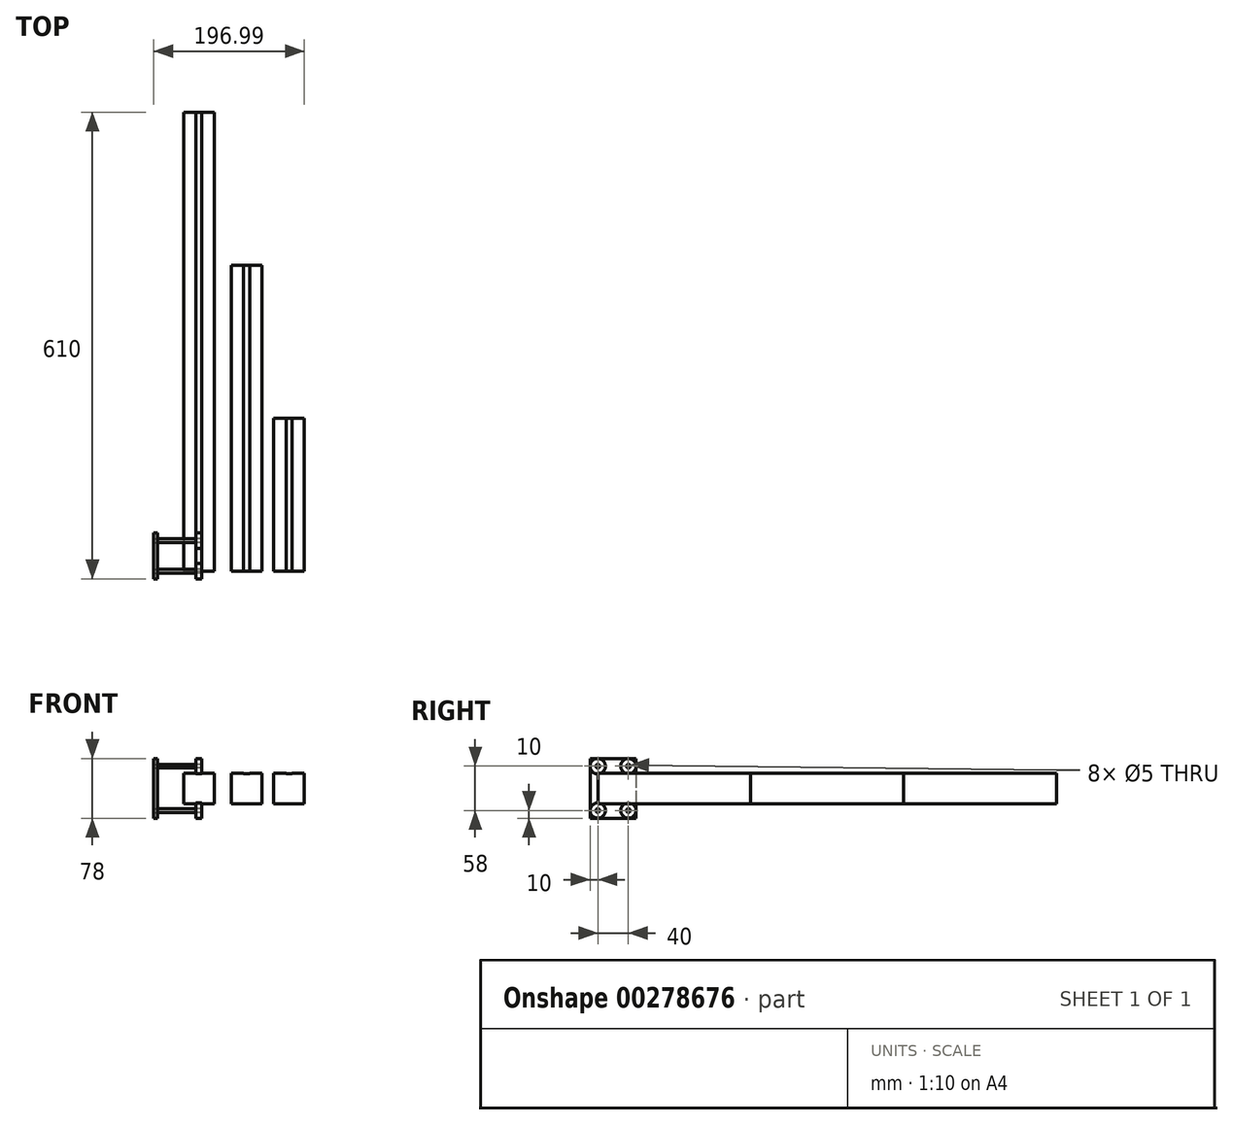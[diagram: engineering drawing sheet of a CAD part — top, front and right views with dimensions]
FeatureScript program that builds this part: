
annotation { "Feature Type Name" : "Feature", "Feature Type Description" : "" }
export const myFeature = defineFeature(function(context is Context, id is Id, definition is map)
    precondition{}
    {
        {
            var Q0;
            Q0=qCreatedBy(makeId("Front.planeOp"),FACE);
            var sketch = newSketch(context, id + "F0", { "sketchPlane" : qUnion([Q0])});
            skLineSegment(sketch, "E0.bottom", {"start": v(-20, 20) * mm, "end": v(-4, 20) * mm});
            skLineSegment(sketch, "E0.top", {"start": v(-20, -20) * mm, "end": v(20, -20) * mm});
            skLineSegment(sketch, "E0.left", {"start": v(-20, 20) * mm, "end": v(-20, -20) * mm});
            skLineSegment(sketch, "E0.right", {"start": v(20, 20) * mm, "end": v(20, -20) * mm});
            skPoint(sketch, "E0.middle", {"position": v(0, 0) * mm});
            skLineSegment(sketch, "E1", {"start": v(-4, 19) * mm, "end": v(4, 19) * mm});
            skPoint(sketch, "E2", {"position": v(0, 19) * mm});
            skPoint(sketch, "E2.positionSnap0", {"position": v(0, 20) * mm});
            skLineSegment(sketch, "E3", {"start": v(-4, 19) * mm, "end": v(-4, 20) * mm});
            skLineSegment(sketch, "E4", {"start": v(4, 19) * mm, "end": v(4, 20) * mm});
            skLineSegment(sketch, "E5.trimOffspring", {"start": v(4, 20) * mm, "end": v(20, 20) * mm});
            skLineSegment(sketch, "E6.bottom", {"start": v(-82.6, 20) * mm, "end": v(-66.6, 20) * mm});
            skLineSegment(sketch, "E6.top", {"start": v(-82.6, -20) * mm, "end": v(-42.6, -20) * mm});
            skLineSegment(sketch, "E6.left", {"start": v(-82.6, 20) * mm, "end": v(-82.6, -20) * mm});
            skLineSegment(sketch, "E6.right", {"start": v(-42.6, 20) * mm, "end": v(-42.6, -20) * mm});
            skPoint(sketch, "E6.middle", {"position": v(-62.6, 0) * mm});
            skLineSegment(sketch, "E7", {"start": v(-66.6, 19) * mm, "end": v(-58.6, 19) * mm});
            skPoint(sketch, "E8", {"position": v(-62.6, 19) * mm});
            skPoint(sketch, "E8.positionSnap0", {"position": v(-62.6, 20) * mm});
            skLineSegment(sketch, "E9", {"start": v(-66.6, 19) * mm, "end": v(-66.6, 20) * mm});
            skLineSegment(sketch, "E10", {"start": v(-58.6, 19) * mm, "end": v(-58.6, 20) * mm});
            skLineSegment(sketch, "E11.trimOffspring", {"start": v(-58.6, 20) * mm, "end": v(-42.6, 20) * mm});
            skLineSegment(sketch, "E12.bottom", {"start": v(35.4, 20) * mm, "end": v(51.4, 20) * mm});
            skLineSegment(sketch, "E12.top", {"start": v(35.4, -20) * mm, "end": v(75.4, -20) * mm});
            skLineSegment(sketch, "E12.left", {"start": v(35.4, 20) * mm, "end": v(35.4, -20) * mm});
            skLineSegment(sketch, "E12.right", {"start": v(75.4, 20) * mm, "end": v(75.4, -20) * mm});
            skPoint(sketch, "E12.middle", {"position": v(55.4, 0) * mm});
            skLineSegment(sketch, "E13", {"start": v(51.4, 19) * mm, "end": v(59.4, 19) * mm});
            skPoint(sketch, "E14", {"position": v(55.4, 19) * mm});
            skPoint(sketch, "E14.positionSnap0", {"position": v(55.4, 20) * mm});
            skLineSegment(sketch, "E15", {"start": v(51.4, 19) * mm, "end": v(51.4, 20) * mm});
            skLineSegment(sketch, "E16", {"start": v(59.4, 19) * mm, "end": v(59.4, 20) * mm});
            skLineSegment(sketch, "E17.trimOffspring", {"start": v(59.4, 20) * mm, "end": v(75.4, 20) * mm});
            skSolve(sketch);
        }
        {
            var Q0;
            Q0=makeQuery(id+"F0.imprint","IMPRINT",FACE,{"disambiguationData":[TD([[makeQuery(id+"F0.imprint","IMPRINT",EDGE,{"derivedFrom":sQuery(id+"F0.wireOp",EDGE,"E6.bottom")}),-1.0]])]});
            extrude(context, id + "F1", {"entities" : qUnion([Q0]), "oppositeDirection" : true, "depth" : 600 * mm});
        }
        {
            var Q0;
            Q0=makeQuery(id+"F0.imprint","IMPRINT",FACE,{"disambiguationData":[TD([[makeQuery(id+"F0.imprint","IMPRINT",EDGE,{"derivedFrom":sQuery(id+"F0.wireOp",EDGE,"E0.bottom")}),-1.0]])]});
            extrude(context, id + "F2", {"entities" : qUnion([Q0]), "oppositeDirection" : true, "depth" : 400 * mm});
        }
        {
            var Q0;
            Q0=makeQuery(id+"F0.imprint","IMPRINT",FACE,{"disambiguationData":[TD([[makeQuery(id+"F0.imprint","IMPRINT",EDGE,{"derivedFrom":sQuery(id+"F0.wireOp",EDGE,"E12.bottom")}),-1.0]])]});
            extrude(context, id + "F3", {"entities" : qUnion([Q0]), "oppositeDirection" : true, "depth" : 200 * mm});
        }
        {
            var Q0;
            Q0=makeQuery(id+"F0.imprint","IMPRINT",FACE,{"disambiguationData":[TD([[makeQuery(id+"F0.imprint","IMPRINT",EDGE,{"derivedFrom":sQuery(id+"F0.wireOp",EDGE,"E6.bottom")}),-1.0]])]});
            var sketch = newSketch(context, id + "F4", { "sketchPlane" : qUnion([Q0])});
            skLineSegment(sketch, "E18", {"start": v(-69.2, 29) * mm, "end": v(-55.7, 29) * mm, "construction": true});
            skLineSegment(sketch, "E19", {"start": v(-66.6, 19) * mm, "end": v(-66.6, 26.5) * mm});
            skLineSegment(sketch, "E20", {"start": v(-58.6, 26.5) * mm, "end": v(-58.6, 19) * mm});
            skLineSegment(sketch, "E21", {"start": v(-66.6, 19) * mm, "end": v(-58.6, 19) * mm});
            skLineSegment(sketch, "E22", {"start": v(-66.6, 26.5) * mm, "end": v(-58.6, 26.5) * mm});
            skPoint(sketch, "E23.orphan", {"position": v(-58.6, 29) * mm});
            skSolve(sketch);
        }
        {
            var Q0;
            {var subQ0=sQuery(id+"F4.wireOp",EDGE,"E21");Q0=makeQuery(id+"F4.imprint","IMPRINT",FACE,{"disambiguationData":[TD([[makeQuery(id+"F4.imprint","IMPRINT",EDGE,{"derivedFrom":subQ0}),1.0]])]});}
            var Q1;
            Q1=sQuery(id+"F4.wireOp",EDGE,"E18");
            revolve(context, id + "F5", {"entities" : qUnion([Q0]), "axis" : qUnion([Q1]), "revolveType" : RevolveType.FULL});
        }
        {
            var Q0;
            Q0=makeQuery(id+"F5.opRevolve","SWEPT_FACE",FACE,{"disambiguationData":[OSD([sQuery(id+"F4.wireOp",EDGE,"E19")])]});
            var sketch = newSketch(context, id + "F6", { "sketchPlane" : qUnion([Q0])});
            skCircle(sketch, "E24.0.0", {"center": v(0, 29) * mm, "radius": 10 * mm});
            skSolve(sketch);
        }
        {
            var Q0;
            Q0=makeQuery(id+"F6.imprint","IMPRINT",FACE,{"disambiguationData":[TD([[makeQuery(id+"F6.imprint","IMPRINT",EDGE,{"derivedFrom":makeQuery(id+"F5.opRevolve","SWEPT_EDGE",EDGE,{"disambiguationData":[OSD([sQuery(id+"F4.wireOp",EDGE,"E19"),sQuery(id+"F4.wireOp",EDGE,"E22")])]})}),1.0]])]});
            extrude(context, id + "F7", {"entities" : qUnion([Q0]), "depth" : 50 * mm});
        }
        {
            var Q0;
            Q0=makeQuery(id+"F7.opExtrude","SWEPT_BODY",BODY,{"disambiguationData":[OSD([sQuery(id+"F4.wireOp",EDGE,"E19"),sQuery(id+"F4.wireOp",EDGE,"E22")])]});
            var Q1;
            Q1=makeQuery(id+"F5.opRevolve","SWEPT_BODY",BODY,{"disambiguationData":[OSD([sQuery(id+"F4.wireOp",EDGE,"E19"),sQuery(id+"F4.wireOp",EDGE,"E20"),sQuery(id+"F4.wireOp",EDGE,"E21"),sQuery(id+"F4.wireOp",EDGE,"E22")])]});
            var Q2;
            Q2=qCreatedBy(makeId("Top.planeOp"),FACE);
            mirror(context, id + "F8", {"entities" : qUnion([Q0, Q1]), "mirrorPlane" : qUnion([Q2])});
        }
        {
            var Q0;
            Q0=makeQuery(id+"F5.opRevolve","SWEPT_BODY",BODY,{"disambiguationData":[OSD([sQuery(id+"F4.wireOp",EDGE,"E19"),sQuery(id+"F4.wireOp",EDGE,"E20"),sQuery(id+"F4.wireOp",EDGE,"E21"),sQuery(id+"F4.wireOp",EDGE,"E22")])]});
            var Q1;
            Q1=makeQuery(id+"F7.opExtrude","SWEPT_BODY",BODY,{"disambiguationData":[OSD([sQuery(id+"F4.wireOp",EDGE,"E19"),sQuery(id+"F4.wireOp",EDGE,"E22")])]});
            var Q2;
            Q2=makeQuery(id+"F8.opPattern","COPY",BODY,{"derivedFrom":makeQuery(id+"F7.opExtrude","SWEPT_BODY",BODY,{"disambiguationData":[OSD([sQuery(id+"F4.wireOp",EDGE,"E19"),sQuery(id+"F4.wireOp",EDGE,"E22")])]}),"instanceName":"1"});
            var Q3;
            Q3=makeQuery(id+"F8.opPattern","COPY",BODY,{"derivedFrom":makeQuery(id+"F5.opRevolve","SWEPT_BODY",BODY,{"disambiguationData":[OSD([sQuery(id+"F4.wireOp",EDGE,"E19"),sQuery(id+"F4.wireOp",EDGE,"E20"),sQuery(id+"F4.wireOp",EDGE,"E21"),sQuery(id+"F4.wireOp",EDGE,"E22")])]}),"instanceName":"1"});
            var Q4;
            Q4=makeQuery(id+"F1.opExtrude","SWEPT_EDGE",EDGE,{"disambiguationData":[OSD([sQuery(id+"F0.wireOp",EDGE,"E6.bottom"),sQuery(id+"F0.wireOp",EDGE,"E6.left")])]});
            transform(context, id + "F9", {"entities" : qUnion([Q0, Q1, Q2, Q3]), "transformType" : TransformType.TRANSLATION_DISTANCE, "transformDirection" : qUnion([Q4]), "distance" : 40 * mm, "oppositeDirection" : true, "makeCopy" : true});
        }
        {
            var Q0;
            Q0=makeQuery(id+"F9.opPattern","COPY",FACE,{"derivedFrom":makeQuery(id+"F7.opExtrude","CAP_FACE",FACE,{"disambiguationData":[OSD([sQuery(id+"F4.wireOp",EDGE,"E19"),sQuery(id+"F4.wireOp",EDGE,"E22")])],"isStart":false}),"instanceName":"1"});
            var sketch = newSketch(context, id + "F10", { "sketchPlane" : qUnion([Q0])});
            skCircle(sketch, "E25.0", {"center": v(-40, 29) * mm, "radius": 2.5 * mm});
            skCircle(sketch, "E26.0", {"center": v(0, 29) * mm, "radius": 2.5 * mm});
            skCircle(sketch, "E27.0", {"center": v(-40, -29) * mm, "radius": 2.5 * mm});
            skCircle(sketch, "E28.0", {"center": v(0, -29) * mm, "radius": 2.5 * mm});
            skLineSegment(sketch, "E29.bottom", {"start": v(-50, 39) * mm, "end": v(10, 39) * mm});
            skLineSegment(sketch, "E29.top", {"start": v(-50, -39) * mm, "end": v(10, -39) * mm});
            skLineSegment(sketch, "E29.left", {"start": v(-50, 39) * mm, "end": v(-50, -39) * mm});
            skLineSegment(sketch, "E29.right", {"start": v(10, 39) * mm, "end": v(10, -39) * mm});
            skSolve(sketch);
        }
        {
            var Q0;
            Q0=makeQuery(id+"F10.imprint","IMPRINT",FACE,{"disambiguationData":[TD([[makeQuery(id+"F10.imprint","IMPRINT",EDGE,{"derivedFrom":sQuery(id+"F10.wireOp",EDGE,"E25.0")}),-1.0]])]});
            extrude(context, id + "F11", {"entities" : qUnion([Q0]), "depth" : 5 * mm});
        }
    });
